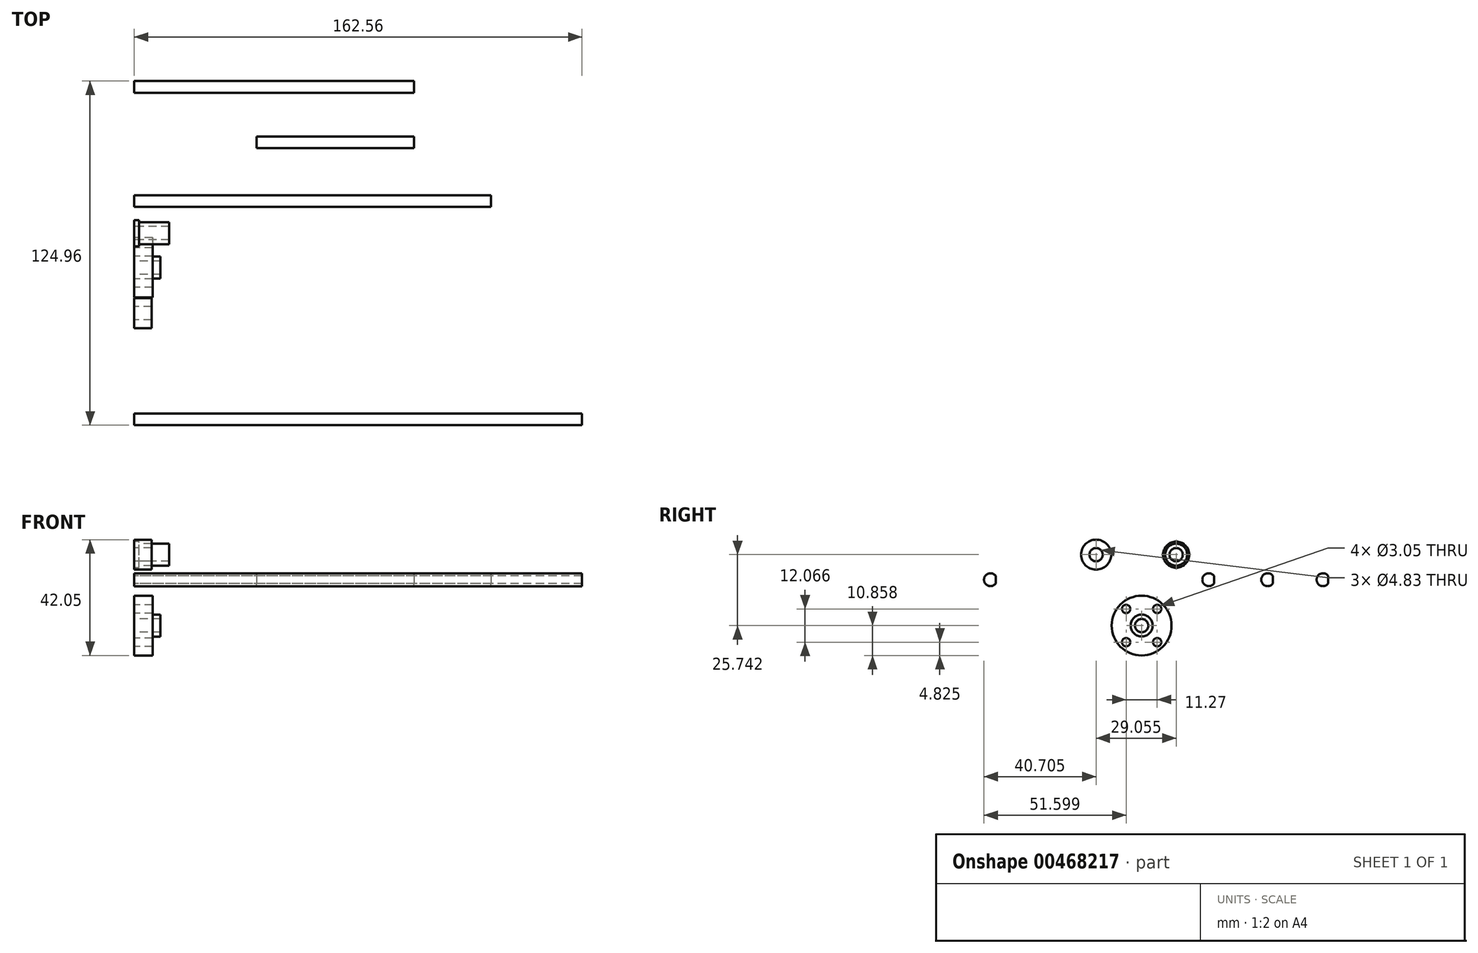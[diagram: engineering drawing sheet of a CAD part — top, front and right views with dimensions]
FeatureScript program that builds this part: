
annotation { "Feature Type Name" : "Feature", "Feature Type Description" : "" }
export const myFeature = defineFeature(function(context is Context, id is Id, definition is map)
    precondition{}
    {
        {
            var Q0;
            Q0=qCreatedBy(makeId("Right.planeOp"),FACE);
            var sketch = newSketch(context, id + "F0", { "sketchPlane" : qUnion([Q0])});
            skCircle(sketch, "E0", {"center": v(0, 0) * mm, "radius": 4.76 * mm});
            skCircle(sketch, "E1", {"center": v(0, 0) * mm, "radius": 3.99 * mm});
            skCircle(sketch, "E2", {"center": v(0, 0) * mm, "radius": 2.41 * mm});
            skSolve(sketch);
        }
        {
            var Q0;
            Q0=makeQuery(id+"F0.imprint","IMPRINT",FACE,{"disambiguationData":[TD([[makeQuery(id+"F0.imprint","IMPRINT",EDGE,{"derivedFrom":sQuery(id+"F0.wireOp",EDGE,"E0")}),1.0]])]});
            extrude(context, id + "F1", {"entities" : qUnion([Q0]), "depth" : 1.68 * mm});
        }
        {
            var Q0;
            Q0=makeQuery(id+"F0.imprint","IMPRINT",FACE,{"disambiguationData":[TD([[makeQuery(id+"F0.imprint","IMPRINT",EDGE,{"derivedFrom":sQuery(id+"F0.wireOp",EDGE,"E1")}),1.0]])]});
            extrude(context, id + "F2", {"entities" : qUnion([Q0]), "operationType" : NewBodyOperationType.ADD, "depth" : 12.7 * mm});
        }
        {
            var Q0;
            Q0=qCreatedBy(makeId("Right.planeOp"),FACE);
            var sketch = newSketch(context, id + "F3", { "sketchPlane" : qUnion([Q0])});
            skCircle(sketch, "E3", {"center": v(-29.05, 0) * mm, "radius": 2.41 * mm});
            skCircle(sketch, "E4", {"center": v(-29.05, 0) * mm, "radius": 5.45 * mm});
            skSolve(sketch);
        }
        {
            var Q0;
            Q0=makeQuery(id+"F3.imprint","IMPRINT",FACE,{"disambiguationData":[TD([[makeQuery(id+"F3.imprint","IMPRINT",EDGE,{"derivedFrom":sQuery(id+"F3.wireOp",EDGE,"E3")}),-1.0]])]});
            extrude(context, id + "F4", {"entities" : qUnion([Q0]), "depth" : 6.35 * mm});
        }
        {
            var Q0;
            Q0=qCreatedBy(makeId("Right.planeOp"),FACE);
            var sketch = newSketch(context, id + "F5", { "sketchPlane" : qUnion([Q0])});
            skCircle(sketch, "E5", {"center": v(-12.53, -25.74) * mm, "radius": 10.86 * mm});
            skCircle(sketch, "E6", {"center": v(-12.53, -25.74) * mm, "radius": 2.41 * mm});
            skSolve(sketch);
        }
        {
            var Q0;
            Q0=makeQuery(id+"F5.imprint","IMPRINT",FACE,{"disambiguationData":[TD([[makeQuery(id+"F5.imprint","IMPRINT",EDGE,{"derivedFrom":sQuery(id+"F5.wireOp",EDGE,"E5")}),1.0]])]});
            extrude(context, id + "F6", {"entities" : qUnion([Q0]), "depth" : 6.73 * mm});
        }
        {
            var Q0;
            Q0=makeQuery(id+"F6.opExtrude","CAP_FACE",FACE,{"disambiguationData":[OSD([sQuery(id+"F5.wireOp",EDGE,"E5"),sQuery(id+"F5.wireOp",EDGE,"E6")])],"isStart":false});
            var sketch = newSketch(context, id + "F7", { "sketchPlane" : qUnion([Q0])});
            skCircle(sketch, "E7", {"center": v(-12.53, -25.74) * mm, "radius": 4 * mm});
            skSolve(sketch);
        }
        {
            var Q0;
            Q0=makeQuery(id+"F7.imprint","IMPRINT",FACE,{"disambiguationData":[TD([[makeQuery(id+"F7.imprint","IMPRINT",EDGE,{"derivedFrom":sQuery(id+"F7.wireOp",EDGE,"E7")}),1.0]])]});
            extrude(context, id + "F8", {"entities" : qUnion([Q0]), "operationType" : NewBodyOperationType.ADD, "depth" : 2.8 * mm});
        }
        {
            var Q0;
            Q0=makeQuery(id+"F6.opExtrude","CAP_FACE",FACE,{"disambiguationData":[OSD([sQuery(id+"F5.wireOp",EDGE,"E5"),sQuery(id+"F5.wireOp",EDGE,"E6")])],"isStart":true});
            var sketch = newSketch(context, id + "F9", { "sketchPlane" : qUnion([Q0])});
            skCircle(sketch, "E8", {"center": v(12.53, -25.74) * mm, "radius": 8.26 * mm});
            skLineSegment(sketch, "E9.rect.bottom", {"start": v(18.16, -31.78) * mm, "end": v(6.9, -31.78) * mm});
            skLineSegment(sketch, "E9.rect.top", {"start": v(18.16, -19.7) * mm, "end": v(6.9, -19.7) * mm});
            skLineSegment(sketch, "E9.rect.left", {"start": v(18.16, -31.78) * mm, "end": v(18.16, -19.7) * mm});
            skLineSegment(sketch, "E9.rect.right", {"start": v(6.9, -31.78) * mm, "end": v(6.9, -19.7) * mm});
            skSolve(sketch);
        }
        {
            var Q0;
            Q0=sQuery(id+"F9.wireOp",VERTEX,"E9.rect.right.end");
            var Q1;
            Q1=sQuery(id+"F9.wireOp",VERTEX,"E9.rect.left.end");
            var Q2;
            Q2=sQuery(id+"F9.wireOp",VERTEX,"E9.rect.bottom.start");
            var Q3;
            Q3=sQuery(id+"F9.wireOp",VERTEX,"E9.rect.right.start");
            var Q4;
            Q4=makeQuery(id+"F6.opExtrude","SWEPT_BODY",BODY,{"disambiguationData":[OSD([sQuery(id+"F5.wireOp",EDGE,"E5"),sQuery(id+"F5.wireOp",EDGE,"E6")])]});
            hole(context, id + "F10", {"style" : HoleStyle.SIMPLE, "holeDiameter" : 3.05 * mm, "endStyle" : HoleEndStyle.THROUGH, "locations" : qUnion([Q0, Q1, Q2, Q3]), "scope" : qUnion([Q4])});
        }
        {
            var Q0;
            Q0=qCreatedBy(makeId("Right.planeOp"),FACE);
            var sketch = newSketch(context, id + "F11", { "sketchPlane" : qUnion([Q0])});
            skCircle(sketch, "E10", {"center": v(11.85, -9.1) * mm, "radius": 2.35 * mm});
            skLineSegment(sketch, "E11", {"start": v(13.72, -7.66) * mm, "end": v(13.72, -10.52) * mm});
            skSolve(sketch);
        }
        {
            var Q0;
            {var subQ0=sQuery(id+"F11.wireOp",EDGE,"E11");Q0=makeQuery(id+"F11.imprint","IMPRINT",FACE,{"disambiguationData":[TD([[makeQuery(id+"F11.imprint","IMPRINT",EDGE,{"derivedFrom":subQ0}),-1.0]])]});}
            extrude(context, id + "F12", {"entities" : qUnion([Q0]), "depth" : 129.54 * mm});
        }
        {
            var Q0;
            Q0=makeQuery(id+"F12.opExtrude","SWEPT_BODY",BODY,{"disambiguationData":[OSD([sQuery(id+"F11.wireOp",EDGE,"E10"),sQuery(id+"F11.wireOp",EDGE,"E11")])]});
            transform(context, id + "F13", {"entities" : qUnion([Q0]), "transformType" : TransformType.TRANSLATION_3D, "dx" : 0 * mm, "dy" : 41.48 * mm, "dz" : 0 * mm, "makeCopy" : true});
        }
        {
            var Q0;
            Q0=makeQuery(id+"F13.opPattern","COPY",FACE,{"derivedFrom":makeQuery(id+"F12.opExtrude","CAP_FACE",FACE,{"disambiguationData":[OSD([sQuery(id+"F11.wireOp",EDGE,"E10"),sQuery(id+"F11.wireOp",EDGE,"E11")])],"isStart":false}),"instanceName":"1"});
            extrude(context, id + "F14", {"entities" : qUnion([Q0]), "operationType" : NewBodyOperationType.REMOVE, "oppositeDirection" : true, "depth" : 27.94 * mm});
        }
        {
            var Q0;
            Q0=makeQuery(id+"F12.opExtrude","SWEPT_BODY",BODY,{"disambiguationData":[OSD([sQuery(id+"F11.wireOp",EDGE,"E10"),sQuery(id+"F11.wireOp",EDGE,"E11")])]});
            transform(context, id + "F15", {"entities" : qUnion([Q0]), "transformType" : TransformType.TRANSLATION_3D, "dx" : 0 * mm, "dy" : -79.26 * mm, "dz" : 0 * mm, "makeCopy" : true});
        }
        {
            var Q0;
            Q0=makeQuery(id+"F15.opPattern","COPY",FACE,{"derivedFrom":makeQuery(id+"F12.opExtrude","CAP_FACE",FACE,{"disambiguationData":[OSD([sQuery(id+"F11.wireOp",EDGE,"E10"),sQuery(id+"F11.wireOp",EDGE,"E11")])],"isStart":false}),"instanceName":"1"});
            extrude(context, id + "F16", {"entities" : qUnion([Q0]), "operationType" : NewBodyOperationType.ADD, "depth" : 33.02 * mm});
        }
        {
            var Q0;
            Q0=makeQuery(id+"F13.opPattern","COPY",BODY,{"derivedFrom":makeQuery(id+"F12.opExtrude","SWEPT_BODY",BODY,{"disambiguationData":[OSD([sQuery(id+"F11.wireOp",EDGE,"E10"),sQuery(id+"F11.wireOp",EDGE,"E11")])]}),"instanceName":"1"});
            transform(context, id + "F17", {"entities" : qUnion([Q0]), "transformType" : TransformType.TRANSLATION_3D, "dx" : 0 * mm, "dy" : -20.08 * mm, "dz" : 0 * mm, "makeCopy" : true});
        }
        {
            var Q0;
            Q0=makeQuery(id+"F17.opPattern","COPY",FACE,{"derivedFrom":makeQuery(id+"F13.opPattern","COPY",FACE,{"derivedFrom":makeQuery(id+"F12.opExtrude","CAP_FACE",FACE,{"disambiguationData":[OSD([sQuery(id+"F11.wireOp",EDGE,"E10"),sQuery(id+"F11.wireOp",EDGE,"E11")])],"isStart":true}),"instanceName":"1"}),"instanceName":"1"});
            extrude(context, id + "F18", {"entities" : qUnion([Q0]), "operationType" : NewBodyOperationType.REMOVE, "oppositeDirection" : true, "depth" : 44.45 * mm});
        }
    });
